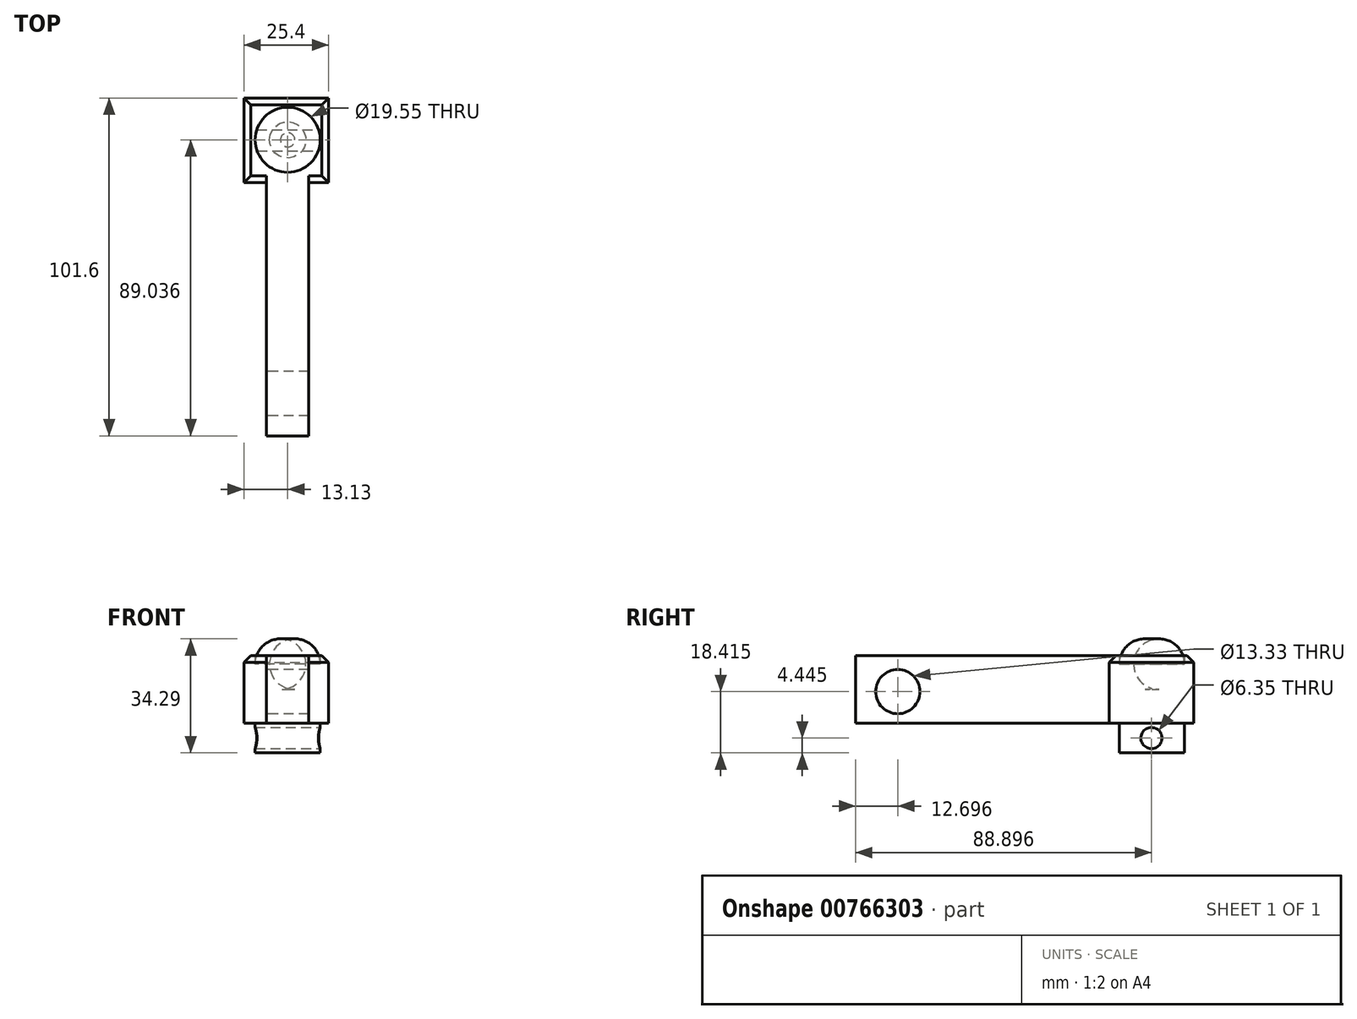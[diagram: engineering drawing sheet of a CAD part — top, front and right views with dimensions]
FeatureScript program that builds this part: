
annotation { "Feature Type Name" : "Feature", "Feature Type Description" : "" }
export const myFeature = defineFeature(function(context is Context, id is Id, definition is map)
    precondition{}
    {
        {
            var Q0;
            Q0=qCreatedBy(makeId("Top.planeOp"),FACE);
            var sketch = newSketch(context, id + "F0", { "sketchPlane" : qUnion([Q0])});
            skLineSegment(sketch, "E0.bottom", {"start": v(0, 63.4) * mm, "end": v(12.7, 63.4) * mm});
            skLineSegment(sketch, "E0.top", {"start": v(0, -12.8) * mm, "end": v(12.7, -12.8) * mm});
            skLineSegment(sketch, "E0.left", {"start": v(0, 63.4) * mm, "end": v(0, -12.8) * mm});
            skLineSegment(sketch, "E0.right", {"start": v(12.7, 63.4) * mm, "end": v(12.7, -12.8) * mm});
            skPoint(sketch, "E1.oppositeSnap0", {"position": v(6.35, 63.4) * mm});
            skLineSegment(sketch, "E1.bottom", {"start": v(-6.78, 88.8) * mm, "end": v(18.62, 88.8) * mm});
            skLineSegment(sketch, "E1.top", {"start": v(-6.78, 63.4) * mm, "end": v(18.62, 63.4) * mm});
            skLineSegment(sketch, "E1.left", {"start": v(-6.78, 88.8) * mm, "end": v(-6.78, 63.4) * mm});
            skLineSegment(sketch, "E1.right", {"start": v(18.62, 88.8) * mm, "end": v(18.62, 63.4) * mm});
            skCircle(sketch, "E2", {"center": v(6.35, 76.25) * mm, "radius": 9.77 * mm});
            skSolve(sketch);
        }
        {
            var Q0;
            Q0=makeQuery(id+"F0.imprint","IMPRINT",FACE,{"disambiguationData":[TD([[makeQuery(id+"F0.imprint","IMPRINT",EDGE,{"derivedFrom":sQuery(id+"F0.wireOp",EDGE,"E1.bottom")}),-1.0]])]});
            var Q1;
            Q1=makeQuery(id+"F0.imprint","IMPRINT",FACE,{"disambiguationData":[TD([[makeQuery(id+"F0.imprint","IMPRINT",EDGE,{"derivedFrom":sQuery(id+"F0.wireOp",EDGE,"E0.top")}),1.0]])]});
            extrude(context, id + "F1", {"entities" : qUnion([Q0, Q1]), "depth" : 20.32 * mm, "offsetDistance" : 25.4 * mm});
        }
        {
            var Q0;
            Q0=makeQuery(id+"F0.imprint","IMPRINT",FACE,{"disambiguationData":[TD([[makeQuery(id+"F0.imprint","IMPRINT",EDGE,{"derivedFrom":sQuery(id+"F0.wireOp",EDGE,"E2")}),1.0]])]});
            extrude(context, id + "F2", {"entities" : qUnion([Q0]), "operationType" : NewBodyOperationType.ADD, "depth" : 10.16 * mm, "offsetDistance" : 25.4 * mm});
        }
        {
            var Q0;
            Q0=makeQuery(id+"F2.opExtrude","CAP_FACE",FACE,{"disambiguationData":[OSD([sQuery(id+"F0.wireOp",EDGE,"E2")])],"isStart":false});
            fillet(context, id + "F3", {"entities" : qUnion([Q0]), "radius" : 7.62 * mm, "tangentPropagation" : true, "allowEdgeOverflow" : false});
        }
        {
            var Q0;
            Q0=makeQuery(id+"F1.opExtrude","SWEPT_FACE",FACE,{"disambiguationData":[OSD([sQuery(id+"F0.wireOp",EDGE,"E0.left")])]});
            var sketch = newSketch(context, id + "F4", { "sketchPlane" : qUnion([Q0])});
            skPoint(sketch, "E3", {"position": v(0.1, 9.53) * mm});
            skPoint(sketch, "E3.positionSnap0", {"position": v(4.84, 12.7) * mm});
            skSolve(sketch);
        }
        {
            var Q0;
            Q0=sQuery(id+"F4.wireOp",VERTEX,"E3");
            var Q1;
            Q1=makeQuery(id+"F1.opExtrude","SWEPT_BODY",BODY,{"disambiguationData":[OSD([sQuery(id+"F0.wireOp",EDGE,"E0.top"),sQuery(id+"F0.wireOp",EDGE,"E0.left"),sQuery(id+"F0.wireOp",EDGE,"E0.right"),sQuery(id+"F0.wireOp",EDGE,"E1.bottom"),sQuery(id+"F0.wireOp",EDGE,"E1.top"),sQuery(id+"F0.wireOp",EDGE,"E1.left"),sQuery(id+"F0.wireOp",EDGE,"E1.right"),sQuery(id+"F0.wireOp",EDGE,"E2")])]});
            hole(context, id + "F5", {"style" : HoleStyle.SIMPLE, "endStyle" : HoleEndStyle.THROUGH, "holeDiameter" : 13.33 * mm, "majorDiameter" : 6.35 * mm, "isTappedThrough" : true, "tappedDepth" : 12.7 * mm, "tapClearance" : 3, "locations" : qUnion([Q0]), "scope" : qUnion([Q1])});
        }
        {
            var Q0;
            Q0=makeQuery(id+"F1.opExtrude","CAP_EDGE",EDGE,{"disambiguationData":[OSD([sQuery(id+"F0.wireOp",EDGE,"E1.left")])],"isStart":false});
            var Q1;
            Q1=makeQuery(id+"F1.opExtrude","CAP_EDGE",EDGE,{"disambiguationData":[OSD([sQuery(id+"F0.wireOp",EDGE,"E1.right")])],"isStart":false});
            var Q2;
            {var subQ0=sQuery(id+"F0.wireOp",EDGE,"E1.top");Q2=makeQuery(id+"F1.opExtrude","CAP_EDGE",EDGE,{"disambiguationData":[OSD([subQ0]),TDD([makeQuery(id+"F0.imprint","IMPRINT",EDGE,{"disambiguationData":[TD([[makeQuery(id+"F0.imprint","INTERSECT",VERTEX,{"derivedFrom":[sQuery(id+"F0.wireOp",EDGE,"E0.left"),subQ0]}),1.0]])],"derivedFrom":subQ0})])],"isStart":false});}
            var Q3;
            {var subQ0=sQuery(id+"F0.wireOp",EDGE,"E1.top");Q3=makeQuery(id+"F1.opExtrude","CAP_EDGE",EDGE,{"disambiguationData":[OSD([subQ0]),TDD([makeQuery(id+"F0.imprint","IMPRINT",EDGE,{"disambiguationData":[TD([[makeQuery(id+"F0.imprint","INTERSECT",VERTEX,{"derivedFrom":[sQuery(id+"F0.wireOp",EDGE,"E0.right"),subQ0]}),-1.0]])],"derivedFrom":subQ0})])],"isStart":false});}
            var Q4;
            Q4=makeQuery(id+"F1.opExtrude","CAP_EDGE",EDGE,{"disambiguationData":[OSD([sQuery(id+"F0.wireOp",EDGE,"E1.bottom")])],"isStart":false});
            chamfer(context, id + "F6", {"entities" : qUnion([Q0, Q1, Q2, Q3, Q4]), "width" : 2.03 * mm, "tangentPropagation" : true});
        }
        {
            var Q0;
            Q0=makeQuery(id+"F0.imprint","IMPRINT",FACE,{"disambiguationData":[TD([[makeQuery(id+"F0.imprint","IMPRINT",EDGE,{"derivedFrom":sQuery(id+"F0.wireOp",EDGE,"E2")}),1.0]])]});
            extrude(context, id + "F7", {"entities" : qUnion([Q0]), "operationType" : NewBodyOperationType.ADD, "oppositeDirection" : true, "depth" : 8.9 * mm, "offsetDistance" : 25.4 * mm});
        }
        {
            var Q0;
            Q0=makeQuery(id+"F1.opExtrude","SWEPT_FACE",FACE,{"disambiguationData":[OSD([sQuery(id+"F0.wireOp",EDGE,"E1.right")])]});
            var sketch = newSketch(context, id + "F8", { "sketchPlane" : qUnion([Q0])});
            skPoint(sketch, "E4", {"position": v(76.1, -4.45) * mm});
            skPoint(sketch, "E4.positionSnap0", {"position": v(76.1, 0) * mm});
            skSolve(sketch);
        }
        {
            var Q0;
            Q0=sQuery(id+"F8.wireOp",VERTEX,"E4");
            var Q1;
            Q1=makeQuery(id+"F1.opExtrude","SWEPT_BODY",BODY,{"disambiguationData":[OSD([sQuery(id+"F0.wireOp",EDGE,"E0.top"),sQuery(id+"F0.wireOp",EDGE,"E0.left"),sQuery(id+"F0.wireOp",EDGE,"E0.right"),sQuery(id+"F0.wireOp",EDGE,"E1.bottom"),sQuery(id+"F0.wireOp",EDGE,"E1.top"),sQuery(id+"F0.wireOp",EDGE,"E1.left"),sQuery(id+"F0.wireOp",EDGE,"E1.right"),sQuery(id+"F0.wireOp",EDGE,"E2")])]});
            hole(context, id + "F9", {"style" : HoleStyle.SIMPLE, "endStyle" : HoleEndStyle.THROUGH, "holeDiameter" : 6.35 * mm, "majorDiameter" : 6.35 * mm, "isTappedThrough" : true, "tappedDepth" : 12.7 * mm, "tapClearance" : 3, "locations" : qUnion([Q0]), "scope" : qUnion([Q1])});
        }
    });
